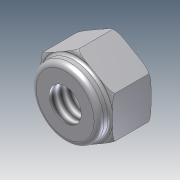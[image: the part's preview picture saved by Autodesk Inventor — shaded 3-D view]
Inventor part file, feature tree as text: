
AUTODESK INVENTOR PART (.ipt)
format: ipt  version: 2012 (Build 160160000, 160)  size: 161,280 bytes
history: native  units: in
note: dims shown in document units (in); Inventor stores cm internally (conversion verified against a paired STEP export)
features: sketch x3, extrude x2, fillet x2, plane x1, revolve x1, hole x1, projected_geometry x1
ambient origin geometry x8: Origin, YZ Plane, XZ Plane, XY Plane, X Axis, Y Axis, Z Axis, Center Point
bodies: Solid1 (feature_tree)
feature tree (11):
  extrude  "Extrusion1"  Depth=0.235in TaperAngle=0.0deg
  plane  "Work Plane1"
  revolve  "Revolution1"  [1 undecoded]
  extrude  "Extrusion2"  TaperAngle=90.0deg  [1 undecoded]
  fillet  "Fillet1"  Radius=0.413in
  fillet  "Fillet2"  Radius=0.07in
  hole  "Hole1"  [1 undecoded]
  sketch  "Sketch1"  dims[d0=0.4375in d1=0.235in d2=0.0in]
  sketch  "Sketch3"  dims[d4=0.04in d5=0.03in]
  sketch  "Sketch4"  dims[d6=0.03in d7=90.0deg d8=0.413in d9=0.07in d10=0.0in d11=0.03in d12=0.015in d13=1.0in d14=1.0in d15=0.196in d16=0.5in d17=0.375in d18=0.25in d19=0.5635in d20=0.75in d21=0.8108in]
  projected_geometry  "Project Cut Edges1"
note: 3 required parameter values undecoded (feature->parameter linkage not recoverable at this tier; creation-order binding heuristic only, values carry confidence <= 0.55)